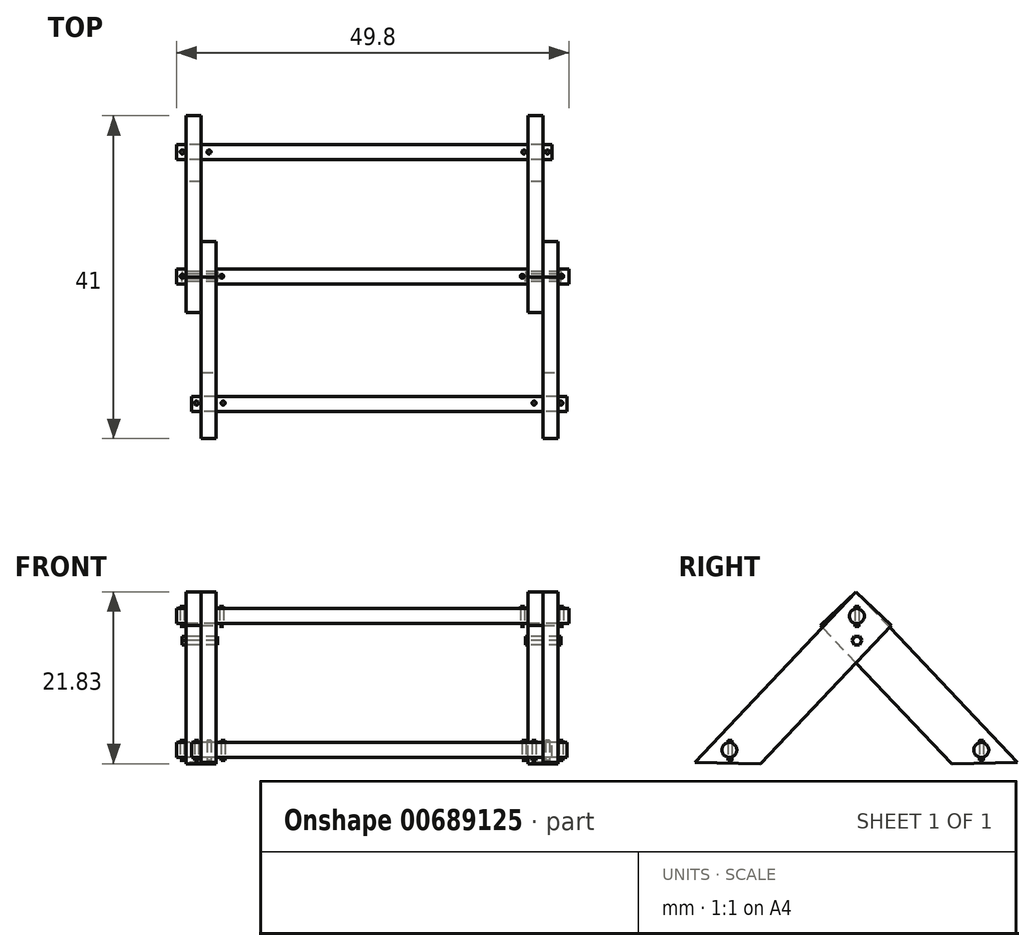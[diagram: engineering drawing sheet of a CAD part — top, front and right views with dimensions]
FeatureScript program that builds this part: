
annotation { "Feature Type Name" : "Feature", "Feature Type Description" : "" }
export const myFeature = defineFeature(function(context is Context, id is Id, definition is map)
    precondition{}
    {
        {
            var Q0;
            Q0=qCreatedBy(makeId("Right.planeOp"),FACE);
            var sketch = newSketch(context, id + "F0", { "sketchPlane" : qUnion([Q0])});
            skLineSegment(sketch, "E0.top", {"start": v(0, 29.8) * mm, "end": v(-6.2, 29.8) * mm});
            skLineSegment(sketch, "E0.left", {"start": v(0, 0) * mm, "end": v(0, 29.8) * mm});
            skLineSegment(sketch, "E0.right", {"start": v(-6.2, 5.6) * mm, "end": v(-6.2, 29.8) * mm});
            skPoint(sketch, "E1", {"position": v(-6.2, 5.6) * mm});
            skLineSegment(sketch, "E2", {"start": v(-6.2, 5.6) * mm, "end": v(0, 0) * mm});
            skPoint(sketch, "E0.bottom.end.orphan", {"position": v(-6.2, 0) * mm});
            skSolve(sketch);
        }
        {
            var Q0;
            Q0=makeQuery(id+"F0.imprint","IMPRINT",FACE,{"disambiguationData":[TD([[makeQuery(id+"F0.imprint","IMPRINT",EDGE,{"derivedFrom":sQuery(id+"F0.wireOp",EDGE,"E0.top")}),1.0]])]});
            extrude(context, id + "F1", {"entities" : qUnion([Q0]), "depth" : 1.9 * mm, "offsetDistance" : 25 * mm});
        }
        {
            var Q0;
            Q0=makeQuery(id+"F1.opExtrude","SWEPT_BODY",BODY,{"disambiguationData":[OSD([sQuery(id+"F0.wireOp",EDGE,"E0.top"),sQuery(id+"F0.wireOp",EDGE,"E0.left"),sQuery(id+"F0.wireOp",EDGE,"E0.right"),sQuery(id+"F0.wireOp",EDGE,"E2")])]});
            var Q1;
            Q1=makeQuery(id+"F1.opExtrude","CAP_EDGE",EDGE,{"disambiguationData":[OSD([sQuery(id+"F0.wireOp",EDGE,"E0.right")])],"isStart":false});
            transform(context, id + "F2", {"entities" : qUnion([Q0]), "transformType" : TransformType.ROTATION, "transformAxis" : qUnion([Q1]), "angle" : 180 * degree, "makeCopy" : true});
        }
        {
            var Q0;
            Q0=makeQuery(id+"F2.opPattern","COPY",BODY,{"derivedFrom":makeQuery(id+"F1.opExtrude","SWEPT_BODY",BODY,{"disambiguationData":[OSD([sQuery(id+"F0.wireOp",EDGE,"E0.top"),sQuery(id+"F0.wireOp",EDGE,"E0.left"),sQuery(id+"F0.wireOp",EDGE,"E0.right"),sQuery(id+"F0.wireOp",EDGE,"E2")])]}),"instanceName":"1"});
            var Q1;
            Q1=makeQuery(id+"F2.opPattern","COPY",EDGE,{"derivedFrom":makeQuery(id+"F1.opExtrude","SWEPT_EDGE",EDGE,{"disambiguationData":[OSD([sQuery(id+"F0.wireOp",EDGE,"E0.top"),sQuery(id+"F0.wireOp",EDGE,"E0.right")])]}),"instanceName":"1"});
            transform(context, id + "F3", {"entities" : qUnion([Q0]), "transformType" : TransformType.ROTATION, "transformAxis" : qUnion([Q1]), "angle" : 316.53 * degree, "makeCopy" : false});
        }
        {
            var Q0;
            Q0=makeQuery(id+"F1.opExtrude","SWEPT_BODY",BODY,{"disambiguationData":[OSD([sQuery(id+"F0.wireOp",EDGE,"E0.top"),sQuery(id+"F0.wireOp",EDGE,"E0.left"),sQuery(id+"F0.wireOp",EDGE,"E0.right"),sQuery(id+"F0.wireOp",EDGE,"E2")])]});
            var Q1;
            Q1=makeQuery(id+"F1.opExtrude","SWEPT_EDGE",EDGE,{"disambiguationData":[OSD([sQuery(id+"F0.wireOp",EDGE,"E0.top"),sQuery(id+"F0.wireOp",EDGE,"E0.right")])]});
            transform(context, id + "F4", {"entities" : qUnion([Q0]), "transformType" : TransformType.ROTATION, "transformAxis" : qUnion([Q1]), "angle" : 316.53 * degree, "makeCopy" : false});
        }
        {
            var Q0;
            Q0=makeQuery(id+"F2.opPattern","COPY",BODY,{"derivedFrom":makeQuery(id+"F1.opExtrude","SWEPT_BODY",BODY,{"disambiguationData":[OSD([sQuery(id+"F0.wireOp",EDGE,"E0.top"),sQuery(id+"F0.wireOp",EDGE,"E0.left"),sQuery(id+"F0.wireOp",EDGE,"E0.right"),sQuery(id+"F0.wireOp",EDGE,"E2")])]}),"instanceName":"1"});
            transform(context, id + "F5", {"entities" : qUnion([Q0]), "transformType" : TransformType.TRANSLATION_3D, "dx" : 0 * mm, "dy" : 10.6 * mm, "dz" : -12 * mm, "makeCopy" : false});
        }
        {
            var Q0;
            Q0=makeQuery(id+"F1.opExtrude","SWEPT_BODY",BODY,{"disambiguationData":[OSD([sQuery(id+"F0.wireOp",EDGE,"E0.top"),sQuery(id+"F0.wireOp",EDGE,"E0.left"),sQuery(id+"F0.wireOp",EDGE,"E0.right"),sQuery(id+"F0.wireOp",EDGE,"E2")])]});
            transform(context, id + "F6", {"entities" : qUnion([Q0]), "transformType" : TransformType.TRANSLATION_3D, "dx" : 0 * mm, "dy" : 1.6 * mm, "dz" : -12 * mm, "makeCopy" : false});
        }
        {
            var Q0;
            Q0=qCreatedBy(makeId("Right.planeOp"),FACE);
            var sketch = newSketch(context, id + "F7", { "sketchPlane" : qUnion([Q0])});
            skCircle(sketch, "E3", {"center": v(0, 0) * mm, "radius": 0.95 * mm});
            skSolve(sketch);
        }
        {
            var Q0;
            Q0=makeQuery(id+"F7.imprint","IMPRINT",FACE,{"disambiguationData":[TD([[makeQuery(id+"F7.imprint","IMPRINT",EDGE,{"derivedFrom":sQuery(id+"F7.wireOp",EDGE,"E3")}),1.0]])]});
            extrude(context, id + "F8", {"entities" : qUnion([Q0]), "depth" : 49.8 * mm, "offsetDistance" : 25 * mm});
        }
        {
            var Q0;
            Q0=makeQuery(id+"F8.opExtrude","SWEPT_BODY",BODY,{"disambiguationData":[OSD([sQuery(id+"F7.wireOp",EDGE,"E3")])]});
            transform(context, id + "F9", {"entities" : qUnion([Q0]), "transformType" : TransformType.TRANSLATION_3D, "dx" : -1.2 * mm, "dy" : 0 * mm, "dz" : 19 * mm, "makeCopy" : false});
        }
        {
            var Q0;
            Q0=makeQuery(id+"F1.opExtrude","SWEPT_BODY",BODY,{"disambiguationData":[OSD([sQuery(id+"F0.wireOp",EDGE,"E0.top"),sQuery(id+"F0.wireOp",EDGE,"E0.left"),sQuery(id+"F0.wireOp",EDGE,"E0.right"),sQuery(id+"F0.wireOp",EDGE,"E2")])]});
            var Q1;
            Q1=makeQuery(id+"F2.opPattern","COPY",BODY,{"derivedFrom":makeQuery(id+"F1.opExtrude","SWEPT_BODY",BODY,{"disambiguationData":[OSD([sQuery(id+"F0.wireOp",EDGE,"E0.top"),sQuery(id+"F0.wireOp",EDGE,"E0.left"),sQuery(id+"F0.wireOp",EDGE,"E0.right"),sQuery(id+"F0.wireOp",EDGE,"E2")])]}),"instanceName":"1"});
            transform(context, id + "F10", {"entities" : qUnion([Q0, Q1]), "transformType" : TransformType.TRANSLATION_3D, "dx" : 43.4 * mm, "dy" : 0 * mm, "dz" : 0 * mm, "makeCopy" : true});
        }
        {
            var Q0;
            Q0=qCreatedBy(makeId("Right.planeOp"),FACE);
            var sketch = newSketch(context, id + "F11", { "sketchPlane" : qUnion([Q0])});
            skCircle(sketch, "E4", {"center": v(0, 0) * mm, "radius": 0.95 * mm});
            skSolve(sketch);
        }
        {
            var Q0;
            Q0=makeQuery(id+"F11.imprint","IMPRINT",FACE,{"disambiguationData":[TD([[makeQuery(id+"F11.imprint","IMPRINT",EDGE,{"derivedFrom":sQuery(id+"F11.wireOp",EDGE,"E4")}),1.0]])]});
            extrude(context, id + "F12", {"entities" : qUnion([Q0]), "depth" : 47.7 * mm, "offsetDistance" : 25 * mm});
        }
        {
            var Q0;
            Q0=makeQuery(id+"F12.opExtrude","SWEPT_BODY",BODY,{"disambiguationData":[OSD([sQuery(id+"F11.wireOp",EDGE,"E4")])]});
            transform(context, id + "F13", {"entities" : qUnion([Q0]), "transformType" : TransformType.TRANSLATION_3D, "dx" : .7 * mm, "dy" : -16.2 * mm, "dz" : 2 * mm, "makeCopy" : false});
        }
        {
            var Q0;
            Q0=makeQuery(id+"F12.opExtrude","SWEPT_BODY",BODY,{"disambiguationData":[OSD([sQuery(id+"F11.wireOp",EDGE,"E4")])]});
            transform(context, id + "F14", {"entities" : qUnion([Q0]), "transformType" : TransformType.TRANSLATION_3D, "dx" : -1.9 * mm, "dy" : 32 * mm, "dz" : 0 * mm, "makeCopy" : true});
        }
        {
            var Q0;
            Q0=qCreatedBy(makeId("Top.planeOp"),FACE);
            var sketch = newSketch(context, id + "F15", { "sketchPlane" : qUnion([Q0])});
            skCircle(sketch, "E5", {"center": v(0, 0) * mm, "radius": 0.25 * mm});
            skSolve(sketch);
        }
        {
            var Q0;
            Q0=makeQuery(id+"F15.imprint","IMPRINT",FACE,{"disambiguationData":[TD([[makeQuery(id+"F15.imprint","IMPRINT",EDGE,{"derivedFrom":sQuery(id+"F15.wireOp",EDGE,"E5")}),1.0]])]});
            extrude(context, id + "F16", {"entities" : qUnion([Q0]), "depth" : 2.5 * mm, "offsetDistance" : 25 * mm});
        }
        {
            var Q0;
            Q0=makeQuery(id+"F16.opExtrude","SWEPT_BODY",BODY,{"disambiguationData":[OSD([sQuery(id+"F15.wireOp",EDGE,"E5")])]});
            transform(context, id + "F17", {"entities" : qUnion([Q0]), "transformType" : TransformType.TRANSLATION_3D, "dx" : -0.5 * mm, "dy" : 15.8 * mm, "dz" : 0.7 * mm, "makeCopy" : false});
        }
        {
            var Q0;
            Q0=makeQuery(id+"F16.opExtrude","SWEPT_BODY",BODY,{"disambiguationData":[OSD([sQuery(id+"F15.wireOp",EDGE,"E5")])]});
            transform(context, id + "F18", {"entities" : qUnion([Q0]), "transformType" : TransformType.TRANSLATION_3D, "dx" : 3.4 * mm, "dy" : 0 * mm, "dz" : 0 * mm, "makeCopy" : true});
        }
        {
            var Q0;
            Q0=makeQuery(id+"F16.opExtrude","SWEPT_BODY",BODY,{"disambiguationData":[OSD([sQuery(id+"F15.wireOp",EDGE,"E5")])]});
            var Q1;
            Q1=makeQuery(id+"F18.opPattern","COPY",BODY,{"derivedFrom":makeQuery(id+"F16.opExtrude","SWEPT_BODY",BODY,{"disambiguationData":[OSD([sQuery(id+"F15.wireOp",EDGE,"E5")])]}),"instanceName":"1"});
            transform(context, id + "F19", {"entities" : qUnion([Q0, Q1]), "transformType" : TransformType.TRANSLATION_3D, "dx" : 43.1 * mm, "dy" : 0 * mm, "dz" : 0 * mm, "makeCopy" : true});
        }
        {
            var Q0;
            Q0=makeQuery(id+"F19.opPattern","COPY",BODY,{"derivedFrom":makeQuery(id+"F16.opExtrude","SWEPT_BODY",BODY,{"disambiguationData":[OSD([sQuery(id+"F15.wireOp",EDGE,"E5")])]}),"instanceName":"1"});
            var Q1;
            Q1=makeQuery(id+"F19.opPattern","COPY",BODY,{"derivedFrom":makeQuery(id+"F18.opPattern","COPY",BODY,{"derivedFrom":makeQuery(id+"F16.opExtrude","SWEPT_BODY",BODY,{"disambiguationData":[OSD([sQuery(id+"F15.wireOp",EDGE,"E5")])]}),"instanceName":"1"}),"instanceName":"1"});
            transform(context, id + "F20", {"entities" : qUnion([Q0, Q1]), "transformType" : TransformType.TRANSLATION_3D, "dx" : 1.6 * mm, "dy" : -31.9 * mm, "dz" : 0 * mm, "makeCopy" : false});
        }
        {
            var Q0;
            Q0=makeQuery(id+"F19.opPattern","COPY",BODY,{"derivedFrom":makeQuery(id+"F16.opExtrude","SWEPT_BODY",BODY,{"disambiguationData":[OSD([sQuery(id+"F15.wireOp",EDGE,"E5")])]}),"instanceName":"1"});
            var Q1;
            Q1=makeQuery(id+"F19.opPattern","COPY",BODY,{"derivedFrom":makeQuery(id+"F18.opPattern","COPY",BODY,{"derivedFrom":makeQuery(id+"F16.opExtrude","SWEPT_BODY",BODY,{"disambiguationData":[OSD([sQuery(id+"F15.wireOp",EDGE,"E5")])]}),"instanceName":"1"}),"instanceName":"1"});
            transform(context, id + "F21", {"entities" : qUnion([Q0, Q1]), "transformType" : TransformType.TRANSLATION_3D, "dx" : -42.9 * mm, "dy" : 0 * mm, "dz" : 0 * mm, "makeCopy" : true});
        }
        {
            var Q0;
            Q0=makeQuery(id+"F16.opExtrude","SWEPT_BODY",BODY,{"disambiguationData":[OSD([sQuery(id+"F15.wireOp",EDGE,"E5")])]});
            transform(context, id + "F22", {"entities" : qUnion([Q0]), "transformType" : TransformType.TRANSLATION_3D, "dx" : 0 * mm, "dy" : -15.8 * mm, "dz" : 17 * mm, "makeCopy" : true});
        }
        {
            var Q0;
            Q0=makeQuery(id+"FTgmlr5JD4i8UZF_4.opPattern","COPY",BODY,{"derivedFrom":makeQuery(id+"F16.opExtrude","SWEPT_BODY",BODY,{"disambiguationData":[OSD([sQuery(id+"F15.wireOp",EDGE,"E5")])]}),"instanceName":"1"});
            var Q1;
            Q1=makeQuery(id+"F16.opExtrude","SWEPT_BODY",BODY,{"disambiguationData":[OSD([sQuery(id+"F15.wireOp",EDGE,"E5")])]});
            transform(context, id + "F23", {"entities" : qUnion([Q0, Q1]), "transformType" : TransformType.TRANSLATION_3D, "dx" : 43.4 * mm, "dy" : 0 * mm, "dz" : 0 * mm, "makeCopy" : true});
        }
        {
            var Q0;
            Q0=makeQuery(id+"F23.opPattern","COPY",BODY,{"derivedFrom":makeQuery(id+"F16.opExtrude","SWEPT_BODY",BODY,{"disambiguationData":[OSD([sQuery(id+"F15.wireOp",EDGE,"E5")])]}),"instanceName":"1"});
            transform(context, id + "F24", {"entities" : qUnion([Q0]), "transformType" : TransformType.TRANSLATION_3D, "dx" : 3 * mm, "dy" : 0 * mm, "dz" : 0 * mm, "makeCopy" : true});
        }
        {
            var Q0;
            Q0=makeQuery(id+"F22.opPattern","COPY",BODY,{"derivedFrom":makeQuery(id+"F16.opExtrude","SWEPT_BODY",BODY,{"disambiguationData":[OSD([sQuery(id+"F15.wireOp",EDGE,"E5")])]}),"instanceName":"1"});
            transform(context, id + "F25", {"entities" : qUnion([Q0]), "transformType" : TransformType.TRANSLATION_3D, "dx" : 5 * mm, "dy" : 0 * mm, "dz" : 0 * mm, "makeCopy" : true});
        }
        {
            var Q0;
            Q0=makeQuery(id+"F25.opPattern","COPY",BODY,{"derivedFrom":makeQuery(id+"F22.opPattern","COPY",BODY,{"derivedFrom":makeQuery(id+"F16.opExtrude","SWEPT_BODY",BODY,{"disambiguationData":[OSD([sQuery(id+"F15.wireOp",EDGE,"E5")])]}),"instanceName":"1"}),"instanceName":"1"});
            var Q1;
            Q1=makeQuery(id+"F22.opPattern","COPY",BODY,{"derivedFrom":makeQuery(id+"F16.opExtrude","SWEPT_BODY",BODY,{"disambiguationData":[OSD([sQuery(id+"F15.wireOp",EDGE,"E5")])]}),"instanceName":"1"});
            transform(context, id + "F26", {"entities" : qUnion([Q0, Q1]), "transformType" : TransformType.TRANSLATION_3D, "dx" : 43.2 * mm, "dy" : 0 * mm, "dz" : 0 * mm, "makeCopy" : true});
        }
        {
            var Q0;
            Q0=qCreatedBy(makeId("Right.planeOp"),FACE);
            var sketch = newSketch(context, id + "F27", { "sketchPlane" : qUnion([Q0])});
            skCircle(sketch, "E6.cCircle", {"center": v(0, 10.3) * mm, "radius": 0.55 * mm, "construction": true});
            skLineSegment(sketch, "E6.0", {"start": v(0.32, 9.75) * mm, "end": v(-0.32, 9.75) * mm});
            skLineSegment(sketch, "E6.1", {"start": v(-0.32, 9.75) * mm, "end": v(-0.64, 10.3) * mm});
            skLineSegment(sketch, "E6.2", {"start": v(-0.64, 10.3) * mm, "end": v(-0.32, 10.85) * mm});
            skLineSegment(sketch, "E6.3", {"start": v(-0.32, 10.85) * mm, "end": v(0.32, 10.85) * mm});
            skLineSegment(sketch, "E6.4", {"start": v(0.32, 10.85) * mm, "end": v(0.64, 10.3) * mm});
            skLineSegment(sketch, "E6.5", {"start": v(0.64, 10.3) * mm, "end": v(0.32, 9.75) * mm});
            skPoint(sketch, "E6.0.midPoint", {"position": v(0, 9.75) * mm});
            skSolve(sketch);
        }
        {
            var Q0;
            Q0=makeQuery(id+"F27.imprint","IMPRINT",FACE,{"disambiguationData":[TD([[makeQuery(id+"F27.imprint","IMPRINT",EDGE,{"derivedFrom":sQuery(id+"F27.wireOp",EDGE,"E6.0")}),-1.0]])]});
            extrude(context, id + "F28", {"entities" : qUnion([Q0]), "depth" : 4.5 * mm, "offsetDistance" : 25 * mm});
        }
        {
            var Q0;
            Q0=makeQuery(id+"F28.opExtrude","SWEPT_BODY",BODY,{"disambiguationData":[OSD([sQuery(id+"F27.wireOp",EDGE,"E6.0"),sQuery(id+"F27.wireOp",EDGE,"E6.1"),sQuery(id+"F27.wireOp",EDGE,"E6.2"),sQuery(id+"F27.wireOp",EDGE,"E6.3"),sQuery(id+"F27.wireOp",EDGE,"E6.4"),sQuery(id+"F27.wireOp",EDGE,"E6.5")])]});
            transform(context, id + "F29", {"entities" : qUnion([Q0]), "transformType" : TransformType.TRANSLATION_3D, "dx" : -0.5 * mm, "dy" : 0 * mm, "dz" : 5.6 * mm, "makeCopy" : false});
        }
        {
            var Q0;
            Q0=makeQuery(id+"F28.opExtrude","SWEPT_BODY",BODY,{"disambiguationData":[OSD([sQuery(id+"F27.wireOp",EDGE,"E6.0"),sQuery(id+"F27.wireOp",EDGE,"E6.1"),sQuery(id+"F27.wireOp",EDGE,"E6.2"),sQuery(id+"F27.wireOp",EDGE,"E6.3"),sQuery(id+"F27.wireOp",EDGE,"E6.4"),sQuery(id+"F27.wireOp",EDGE,"E6.5")])]});
            transform(context, id + "F30", {"entities" : qUnion([Q0]), "transformType" : TransformType.TRANSLATION_3D, "dx" : 43.6 * mm, "dy" : 0 * mm, "dz" : 0 * mm, "makeCopy" : true});
        }
    });
